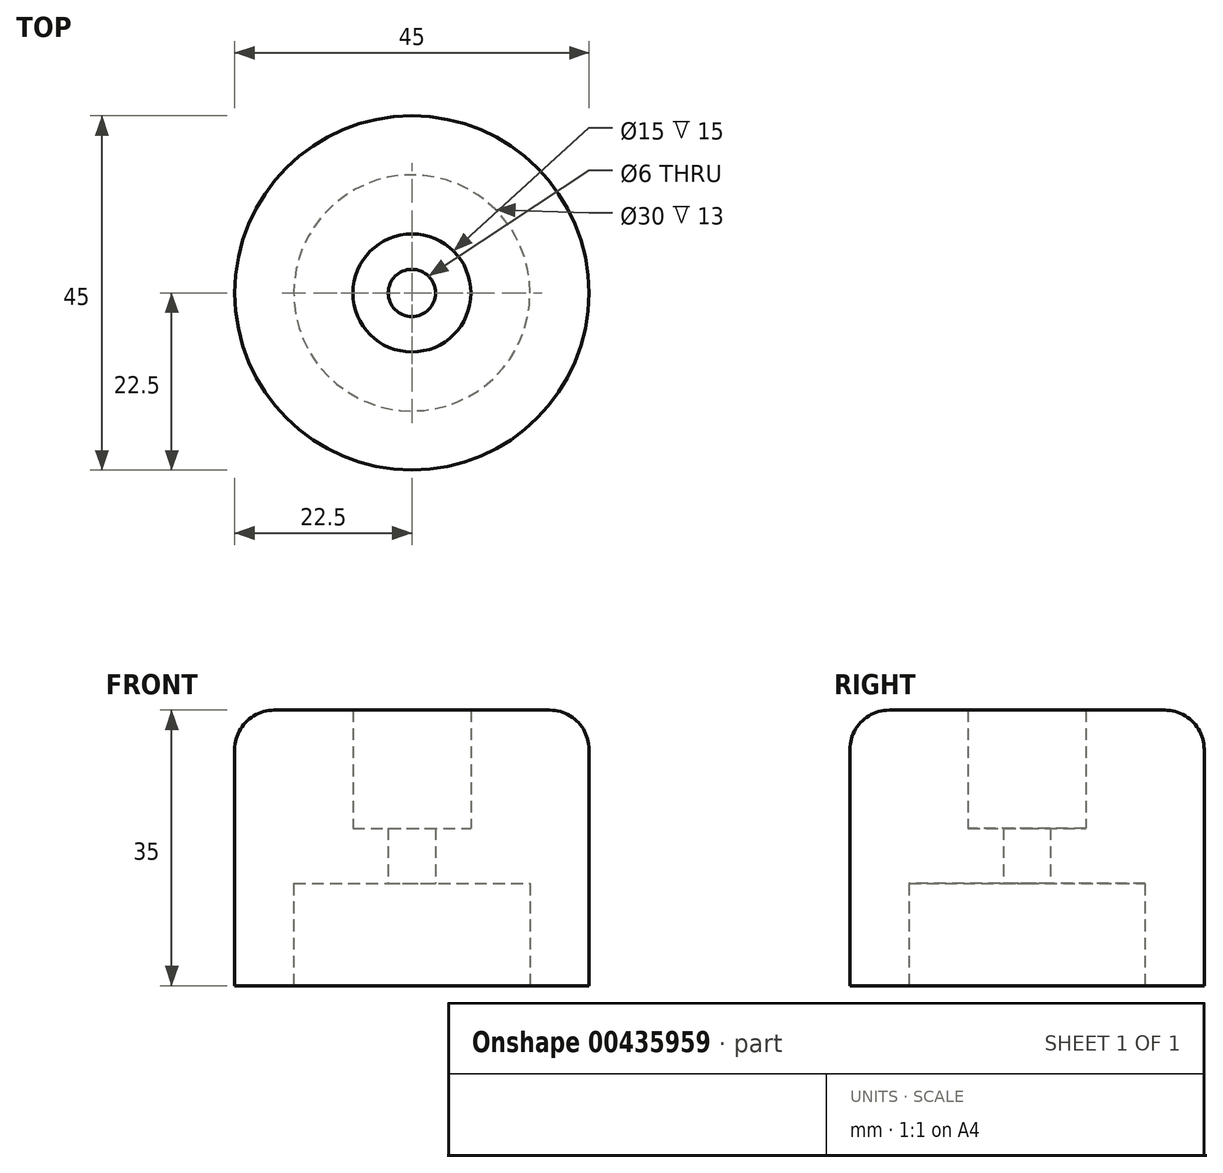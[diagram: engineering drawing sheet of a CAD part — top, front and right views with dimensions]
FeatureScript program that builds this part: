
annotation { "Feature Type Name" : "Feature", "Feature Type Description" : "" }
export const myFeature = defineFeature(function(context is Context, id is Id, definition is map)
    precondition{}
    {
        {
            var Q0;
            Q0=qCreatedBy(makeId("Front.planeOp"),FACE);
            var sketch = newSketch(context, id + "F0", { "sketchPlane" : qUnion([Q0])});
            skLineSegment(sketch, "E0.bottom", {"start": v(0, 0) * mm, "end": v(22.5, 0) * mm});
            skLineSegment(sketch, "E0.top", {"start": v(0, 35) * mm, "end": v(22.5, 35) * mm});
            skLineSegment(sketch, "E0.left", {"start": v(0, 0) * mm, "end": v(0, 35) * mm});
            skLineSegment(sketch, "E0.right", {"start": v(22.5, 0) * mm, "end": v(22.5, 35) * mm});
            skLineSegment(sketch, "E1", {"start": v(3, 35) * mm, "end": v(3, 0) * mm});
            skLineSegment(sketch, "E2", {"start": v(7.5, 35) * mm, "end": v(7.5, 0) * mm});
            skLineSegment(sketch, "E3", {"start": v(15, 35) * mm, "end": v(15, 0) * mm});
            skLineSegment(sketch, "E4", {"start": v(0, 20) * mm, "end": v(22.5, 20) * mm});
            skLineSegment(sketch, "E5", {"start": v(0, 13) * mm, "end": v(22.5, 13) * mm});
            skSolve(sketch);
        }
        {
            var Q0;
            {var subQ0=sQuery(id+"F0.wireOp",EDGE,"E2");var subQ1=sQuery(id+"F0.wireOp",EDGE,"E0.top");var subQ2=makeQuery(id+"F0.imprint","INTERSECT",VERTEX,{"derivedFrom":[subQ1,subQ0]});Q0=makeQuery(id+"F0.imprint","IMPRINT",FACE,{"disambiguationData":[TD([[makeQuery(id+"F0.imprint","IMPRINT",EDGE,{"disambiguationData":[TD([[subQ2,-1.0]])],"derivedFrom":subQ1}),-1.0]])]});}
            var Q1;
            {var subQ0=sQuery(id+"F0.wireOp",EDGE,"E0.right");var subQ1=sQuery(id+"F0.wireOp",EDGE,"E0.top");var subQ2=makeQuery(id+"F0.imprint","INTERSECT",VERTEX,{"derivedFrom":[subQ1,subQ0]});Q1=makeQuery(id+"F0.imprint","IMPRINT",FACE,{"disambiguationData":[TD([[makeQuery(id+"F0.imprint","IMPRINT",EDGE,{"disambiguationData":[TD([[subQ2,1.0]])],"derivedFrom":subQ1}),-1.0]])]});}
            var Q2;
            {var subQ0=sQuery(id+"F0.wireOp",EDGE,"E4");var subQ1=sQuery(id+"F0.wireOp",EDGE,"E0.right");var subQ2=makeQuery(id+"F0.imprint","INTERSECT",VERTEX,{"derivedFrom":[subQ1,subQ0]});Q2=makeQuery(id+"F0.imprint","IMPRINT",FACE,{"disambiguationData":[TD([[makeQuery(id+"F0.imprint","IMPRINT",EDGE,{"disambiguationData":[TD([[subQ2,1.0]])],"derivedFrom":subQ1}),1.0]])]});}
            var Q3;
            {var subQ0=sQuery(id+"F0.wireOp",EDGE,"E4");var subQ1=sQuery(id+"F0.wireOp",EDGE,"E2");var subQ2=makeQuery(id+"F0.imprint","INTERSECT",VERTEX,{"derivedFrom":[subQ1,subQ0]});Q3=makeQuery(id+"F0.imprint","IMPRINT",FACE,{"disambiguationData":[TD([[makeQuery(id+"F0.imprint","IMPRINT",EDGE,{"disambiguationData":[TD([[subQ2,-1.0]])],"derivedFrom":subQ1}),1.0]])]});}
            var Q4;
            {var subQ0=sQuery(id+"F0.wireOp",EDGE,"E4");var subQ1=sQuery(id+"F0.wireOp",EDGE,"E1");var subQ2=makeQuery(id+"F0.imprint","INTERSECT",VERTEX,{"derivedFrom":[subQ1,subQ0]});Q4=makeQuery(id+"F0.imprint","IMPRINT",FACE,{"disambiguationData":[TD([[makeQuery(id+"F0.imprint","IMPRINT",EDGE,{"disambiguationData":[TD([[subQ2,-1.0]])],"derivedFrom":subQ1}),1.0]])]});}
            var Q5;
            {var subQ0=sQuery(id+"F0.wireOp",EDGE,"E0.right");var subQ1=sQuery(id+"F0.wireOp",EDGE,"E0.bottom");var subQ2=makeQuery(id+"F0.imprint","INTERSECT",VERTEX,{"derivedFrom":[subQ1,subQ0]});Q5=makeQuery(id+"F0.imprint","IMPRINT",FACE,{"disambiguationData":[TD([[makeQuery(id+"F0.imprint","IMPRINT",EDGE,{"disambiguationData":[TD([[subQ2,1.0]])],"derivedFrom":subQ1}),1.0]])]});}
            var Q6;
            Q6=sQuery(id+"F0.wireOp",EDGE,"E0.left");
            revolve(context, id + "F1", {"entities" : qUnion([Q0, Q1, Q2, Q3, Q4, Q5]), "axis" : qUnion([Q6]), "revolveType" : RevolveType.FULL});
        }
        {
            var Q0;
            Q0=makeQuery(id+"F1.opRevolve","SWEPT_EDGE",EDGE,{"disambiguationData":[OSD([sQuery(id+"F0.wireOp",EDGE,"E0.top"),sQuery(id+"F0.wireOp",EDGE,"E0.right")])]});
            fillet(context, id + "F2", {"entities" : qUnion([Q0]), "radius" : 5 * mm, "tangentPropagation" : true, "allowEdgeOverflow" : false});
        }
    });
